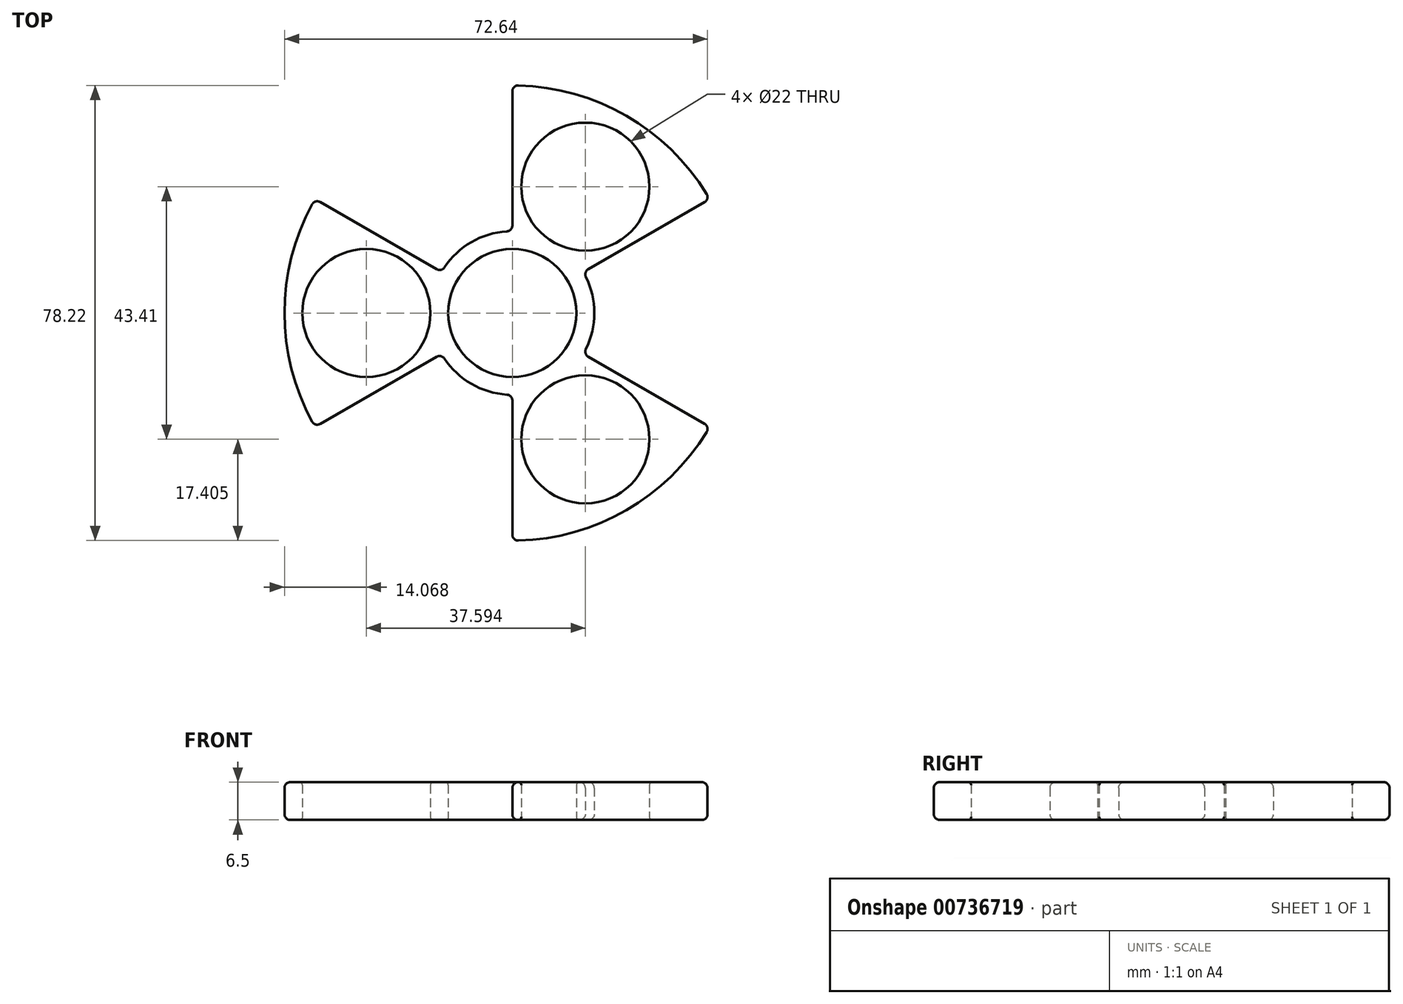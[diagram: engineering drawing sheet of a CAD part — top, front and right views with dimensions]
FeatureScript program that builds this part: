
annotation { "Feature Type Name" : "Feature", "Feature Type Description" : "" }
export const myFeature = defineFeature(function(context is Context, id is Id, definition is map)
    precondition{}
    {
        {
            var Q0;
            Q0=qCreatedBy(makeId("Top.planeOp"),FACE);
            var sketch = newSketch(context, id + "F0", { "sketchPlane" : qUnion([Q0])});
            skCircle(sketch, "E0", {"center": v(0, 0) * mm, "radius": 11 * mm});
            skCircle(sketch, "E1", {"center": v(0, 0) * mm, "radius": 40 * mm});
            skCircle(sketch, "E2", {"center": v(0, 0) * mm, "radius": 39.12 * mm});
            skLineSegment(sketch, "E3", {"start": v(0, 0) * mm, "end": v(0, 40) * mm});
            skLineSegment(sketch, "E4", {"start": v(9.53, -5.5) * mm, "end": v(34.64, -20) * mm});
            skLineSegment(sketch, "E5", {"start": v(-9.53, -5.5) * mm, "end": v(-34.64, -20) * mm});
            skLineSegment(sketch, "E6", {"start": v(-9.53, 5.5) * mm, "end": v(-34.64, 20) * mm});
            skLineSegment(sketch, "E7", {"start": v(9.53, 5.5) * mm, "end": v(34.64, 20) * mm});
            skLineSegment(sketch, "E8", {"start": v(0, 0) * mm, "end": v(0, -40) * mm});
            skCircle(sketch, "E9", {"center": v(0, 0) * mm, "radius": 25.06 * mm});
            skLineSegment(sketch, "E10", {"start": v(5.5, 9.53) * mm, "end": v(20, 34.64) * mm});
            skLineSegment(sketch, "E11", {"start": v(0, 0) * mm, "end": v(-53.49, 0) * mm});
            skLineSegment(sketch, "E12", {"start": v(5.5, -9.53) * mm, "end": v(20, -34.64) * mm});
            skCircle(sketch, "E13", {"center": v(12.53, 21.7) * mm, "radius": 11 * mm});
            skCircle(sketch, "E14", {"center": v(-25.06, 0) * mm, "radius": 11 * mm});
            skCircle(sketch, "E15", {"center": v(12.53, -21.7) * mm, "radius": 11 * mm});
            skPoint(sketch, "E15.perimeterSnap0", {"position": v(13.32, -23.08) * mm});
            skCircle(sketch, "E16", {"center": v(0, 0) * mm, "radius": 17.66 * mm});
            skCircle(sketch, "E17", {"center": v(0, 0) * mm, "radius": 14.06 * mm});
            skSolve(sketch);
        }
        {
            var Q0;
            {var subQ0=sQuery(id+"F0.wireOp",EDGE,"E11");var subQ1=sQuery(id+"F0.wireOp",EDGE,"E2");var subQ2=makeQuery(id+"F0.imprint","INTERSECT",VERTEX,{"derivedFrom":[subQ1,subQ0]});Q0=makeQuery(id+"F0.imprint","IMPRINT",FACE,{"disambiguationData":[TD([[makeQuery(id+"F0.imprint","IMPRINT",EDGE,{"disambiguationData":[TD([[subQ2,-1.0]])],"derivedFrom":subQ1}),1.0]])]});}
            var Q1;
            {var subQ1=sQuery(id+"F0.wireOp",EDGE,"E2");var subQ5=sQuery(id+"F0.wireOp",EDGE,"E6");var subQ6=makeQuery(id+"F0.imprint","INTERSECT",VERTEX,{"derivedFrom":[subQ1,subQ5]});Q1=makeQuery(id+"F0.imprint","IMPRINT",FACE,{"disambiguationData":[TD([[makeQuery(id+"F0.imprint","IMPRINT",EDGE,{"disambiguationData":[TD([[subQ6,-1.0]])],"derivedFrom":subQ1}),1.0]])]});}
            var Q2;
            {var subQ1=sQuery(id+"F0.wireOp",EDGE,"E6");var subQ5=sQuery(id+"F0.wireOp",EDGE,"E0");var subQ6=makeQuery(id+"F0.imprint","INTERSECT",VERTEX,{"derivedFrom":[subQ5,subQ1]});Q2=makeQuery(id+"F0.imprint","IMPRINT",FACE,{"disambiguationData":[TD([[makeQuery(id+"F0.imprint","IMPRINT",EDGE,{"disambiguationData":[TD([[subQ6,-1.0]])],"derivedFrom":subQ5}),-1.0]])]});}
            var Q3;
            {var subQ0=sQuery(id+"F0.wireOp",EDGE,"E11");var subQ1=sQuery(id+"F0.wireOp",EDGE,"E0");var subQ2=makeQuery(id+"F0.imprint","INTERSECT",VERTEX,{"derivedFrom":[subQ1,subQ0]});Q3=makeQuery(id+"F0.imprint","IMPRINT",FACE,{"disambiguationData":[TD([[makeQuery(id+"F0.imprint","IMPRINT",EDGE,{"disambiguationData":[TD([[subQ2,-1.0]])],"derivedFrom":subQ1}),-1.0]])]});}
            var Q4;
            {var subQ0=sQuery(id+"F0.wireOp",EDGE,"E10");var subQ1=sQuery(id+"F0.wireOp",EDGE,"E2");var subQ2=makeQuery(id+"F0.imprint","INTERSECT",VERTEX,{"derivedFrom":[subQ1,subQ0]});Q4=makeQuery(id+"F0.imprint","IMPRINT",FACE,{"disambiguationData":[TD([[makeQuery(id+"F0.imprint","IMPRINT",EDGE,{"disambiguationData":[TD([[subQ2,-1.0]])],"derivedFrom":subQ1}),1.0]])]});}
            var Q5;
            {var subQ5=sQuery(id+"F0.wireOp",EDGE,"E10");var subQ6=sQuery(id+"F0.wireOp",EDGE,"E2");var subQ7=makeQuery(id+"F0.imprint","INTERSECT",VERTEX,{"derivedFrom":[subQ6,subQ5]});Q5=makeQuery(id+"F0.imprint","IMPRINT",FACE,{"disambiguationData":[TD([[makeQuery(id+"F0.imprint","IMPRINT",EDGE,{"disambiguationData":[TD([[subQ7,1.0]])],"derivedFrom":subQ6}),1.0]])]});}
            var Q6;
            {var subQ0=sQuery(id+"F0.wireOp",EDGE,"E10");var subQ1=sQuery(id+"F0.wireOp",EDGE,"E0");var subQ2=makeQuery(id+"F0.imprint","INTERSECT",VERTEX,{"derivedFrom":[subQ1,subQ0]});Q6=makeQuery(id+"F0.imprint","IMPRINT",FACE,{"disambiguationData":[TD([[makeQuery(id+"F0.imprint","IMPRINT",EDGE,{"disambiguationData":[TD([[subQ2,1.0]])],"derivedFrom":subQ1}),-1.0]])]});}
            var Q7;
            {var subQ0=sQuery(id+"F0.wireOp",EDGE,"E10");var subQ1=sQuery(id+"F0.wireOp",EDGE,"E0");var subQ2=makeQuery(id+"F0.imprint","INTERSECT",VERTEX,{"derivedFrom":[subQ1,subQ0]});Q7=makeQuery(id+"F0.imprint","IMPRINT",FACE,{"disambiguationData":[TD([[makeQuery(id+"F0.imprint","IMPRINT",EDGE,{"disambiguationData":[TD([[subQ2,-1.0]])],"derivedFrom":subQ1}),-1.0]])]});}
            var Q8;
            {var subQ0=sQuery(id+"F0.wireOp",EDGE,"E12");var subQ1=sQuery(id+"F0.wireOp",EDGE,"E0");var subQ2=makeQuery(id+"F0.imprint","INTERSECT",VERTEX,{"derivedFrom":[subQ1,subQ0]});Q8=makeQuery(id+"F0.imprint","IMPRINT",FACE,{"disambiguationData":[TD([[makeQuery(id+"F0.imprint","IMPRINT",EDGE,{"disambiguationData":[TD([[subQ2,-1.0]])],"derivedFrom":subQ1}),-1.0]])]});}
            var Q9;
            {var subQ1=sQuery(id+"F0.wireOp",EDGE,"E0");var subQ5=sQuery(id+"F0.wireOp",EDGE,"E8");var subQ6=makeQuery(id+"F0.imprint","INTERSECT",VERTEX,{"derivedFrom":[subQ1,subQ5]});Q9=makeQuery(id+"F0.imprint","IMPRINT",FACE,{"disambiguationData":[TD([[makeQuery(id+"F0.imprint","IMPRINT",EDGE,{"disambiguationData":[TD([[subQ6,-1.0]])],"derivedFrom":subQ1}),-1.0]])]});}
            var Q10;
            {var subQ1=sQuery(id+"F0.wireOp",EDGE,"E2");var subQ5=sQuery(id+"F0.wireOp",EDGE,"E8");var subQ6=makeQuery(id+"F0.imprint","INTERSECT",VERTEX,{"derivedFrom":[subQ1,subQ5]});Q10=makeQuery(id+"F0.imprint","IMPRINT",FACE,{"disambiguationData":[TD([[makeQuery(id+"F0.imprint","IMPRINT",EDGE,{"disambiguationData":[TD([[subQ6,-1.0]])],"derivedFrom":subQ1}),1.0]])]});}
            var Q11;
            {var subQ0=sQuery(id+"F0.wireOp",EDGE,"E3");var subQ1=sQuery(id+"F0.wireOp",EDGE,"E0");var subQ2=makeQuery(id+"F0.imprint","INTERSECT",VERTEX,{"derivedFrom":[subQ1,subQ0]});Q11=makeQuery(id+"F0.imprint","IMPRINT",FACE,{"disambiguationData":[TD([[makeQuery(id+"F0.imprint","IMPRINT",EDGE,{"disambiguationData":[TD([[subQ2,-1.0]])],"derivedFrom":subQ1}),-1.0]])]});}
            var Q12;
            {var subQ0=sQuery(id+"F0.wireOp",EDGE,"E5");var subQ1=sQuery(id+"F0.wireOp",EDGE,"E0");var subQ2=makeQuery(id+"F0.imprint","INTERSECT",VERTEX,{"derivedFrom":[subQ1,subQ0]});Q12=makeQuery(id+"F0.imprint","IMPRINT",FACE,{"disambiguationData":[TD([[makeQuery(id+"F0.imprint","IMPRINT",EDGE,{"disambiguationData":[TD([[subQ2,-1.0]])],"derivedFrom":subQ1}),-1.0]])]});}
            var Q13;
            {var subQ0=sQuery(id+"F0.wireOp",EDGE,"E7");var subQ1=sQuery(id+"F0.wireOp",EDGE,"E0");var subQ2=makeQuery(id+"F0.imprint","INTERSECT",VERTEX,{"derivedFrom":[subQ1,subQ0]});Q13=makeQuery(id+"F0.imprint","IMPRINT",FACE,{"disambiguationData":[TD([[makeQuery(id+"F0.imprint","IMPRINT",EDGE,{"disambiguationData":[TD([[subQ2,1.0]])],"derivedFrom":subQ1}),-1.0]])]});}
            var Q14;
            {var subQ0=sQuery(id+"F0.wireOp",EDGE,"E12");var subQ1=sQuery(id+"F0.wireOp",EDGE,"E2");var subQ2=makeQuery(id+"F0.imprint","INTERSECT",VERTEX,{"derivedFrom":[subQ1,subQ0]});Q14=makeQuery(id+"F0.imprint","IMPRINT",FACE,{"disambiguationData":[TD([[makeQuery(id+"F0.imprint","IMPRINT",EDGE,{"disambiguationData":[TD([[subQ2,-1.0]])],"derivedFrom":subQ1}),1.0]])]});}
            var Q15;
            {var subQ0=sQuery(id+"F0.wireOp",EDGE,"E16");var subQ1=sQuery(id+"F0.wireOp",EDGE,"E6");var subQ2=makeQuery(id+"F0.imprint","INTERSECT",VERTEX,{"derivedFrom":[subQ1,subQ0]});Q15=makeQuery(id+"F0.imprint","IMPRINT",FACE,{"disambiguationData":[TD([[makeQuery(id+"F0.imprint","IMPRINT",EDGE,{"disambiguationData":[TD([[subQ2,-1.0]])],"derivedFrom":subQ1}),1.0]])]});}
            var Q16;
            {var subQ0=sQuery(id+"F0.wireOp",EDGE,"E17");var subQ1=sQuery(id+"F0.wireOp",EDGE,"E6");var subQ2=makeQuery(id+"F0.imprint","INTERSECT",VERTEX,{"derivedFrom":[subQ1,subQ0]});Q16=makeQuery(id+"F0.imprint","IMPRINT",FACE,{"disambiguationData":[TD([[makeQuery(id+"F0.imprint","IMPRINT",EDGE,{"disambiguationData":[TD([[subQ2,-1.0]])],"derivedFrom":subQ1}),1.0]])]});}
            var Q17;
            {var subQ0=sQuery(id+"F0.wireOp",EDGE,"E16");var subQ1=sQuery(id+"F0.wireOp",EDGE,"E5");var subQ2=makeQuery(id+"F0.imprint","INTERSECT",VERTEX,{"derivedFrom":[subQ1,subQ0]});Q17=makeQuery(id+"F0.imprint","IMPRINT",FACE,{"disambiguationData":[TD([[makeQuery(id+"F0.imprint","IMPRINT",EDGE,{"disambiguationData":[TD([[subQ2,-1.0]])],"derivedFrom":subQ1}),-1.0]])]});}
            var Q18;
            {var subQ0=sQuery(id+"F0.wireOp",EDGE,"E17");var subQ1=sQuery(id+"F0.wireOp",EDGE,"E5");var subQ2=makeQuery(id+"F0.imprint","INTERSECT",VERTEX,{"derivedFrom":[subQ1,subQ0]});Q18=makeQuery(id+"F0.imprint","IMPRINT",FACE,{"disambiguationData":[TD([[makeQuery(id+"F0.imprint","IMPRINT",EDGE,{"disambiguationData":[TD([[subQ2,-1.0]])],"derivedFrom":subQ1}),-1.0]])]});}
            var Q19;
            {var subQ0=sQuery(id+"F0.wireOp",EDGE,"E16");var subQ1=sQuery(id+"F0.wireOp",EDGE,"E7");var subQ2=makeQuery(id+"F0.imprint","INTERSECT",VERTEX,{"derivedFrom":[subQ1,subQ0]});Q19=makeQuery(id+"F0.imprint","IMPRINT",FACE,{"disambiguationData":[TD([[makeQuery(id+"F0.imprint","IMPRINT",EDGE,{"disambiguationData":[TD([[subQ2,-1.0]])],"derivedFrom":subQ1}),1.0]])]});}
            var Q20;
            {var subQ0=sQuery(id+"F0.wireOp",EDGE,"E17");var subQ1=sQuery(id+"F0.wireOp",EDGE,"E7");var subQ2=makeQuery(id+"F0.imprint","INTERSECT",VERTEX,{"derivedFrom":[subQ1,subQ0]});Q20=makeQuery(id+"F0.imprint","IMPRINT",FACE,{"disambiguationData":[TD([[makeQuery(id+"F0.imprint","IMPRINT",EDGE,{"disambiguationData":[TD([[subQ2,-1.0]])],"derivedFrom":subQ1}),1.0]])]});}
            var Q21;
            {var subQ0=sQuery(id+"F0.wireOp",EDGE,"E17");var subQ1=sQuery(id+"F0.wireOp",EDGE,"E3");var subQ2=makeQuery(id+"F0.imprint","INTERSECT",VERTEX,{"derivedFrom":[subQ1,subQ0]});Q21=makeQuery(id+"F0.imprint","IMPRINT",FACE,{"disambiguationData":[TD([[makeQuery(id+"F0.imprint","IMPRINT",EDGE,{"disambiguationData":[TD([[subQ2,-1.0]])],"derivedFrom":subQ1}),-1.0]])]});}
            var Q22;
            {var subQ0=sQuery(id+"F0.wireOp",EDGE,"E16");var subQ1=sQuery(id+"F0.wireOp",EDGE,"E3");var subQ2=makeQuery(id+"F0.imprint","INTERSECT",VERTEX,{"derivedFrom":[subQ1,subQ0]});Q22=makeQuery(id+"F0.imprint","IMPRINT",FACE,{"disambiguationData":[TD([[makeQuery(id+"F0.imprint","IMPRINT",EDGE,{"disambiguationData":[TD([[subQ2,-1.0]])],"derivedFrom":subQ1}),-1.0]])]});}
            var Q23;
            {var subQ0=sQuery(id+"F0.wireOp",EDGE,"E17");var subQ1=sQuery(id+"F0.wireOp",EDGE,"E4");var subQ2=makeQuery(id+"F0.imprint","INTERSECT",VERTEX,{"derivedFrom":[subQ1,subQ0]});Q23=makeQuery(id+"F0.imprint","IMPRINT",FACE,{"disambiguationData":[TD([[makeQuery(id+"F0.imprint","IMPRINT",EDGE,{"disambiguationData":[TD([[subQ2,-1.0]])],"derivedFrom":subQ1}),-1.0]])]});}
            var Q24;
            {var subQ0=sQuery(id+"F0.wireOp",EDGE,"E16");var subQ1=sQuery(id+"F0.wireOp",EDGE,"E4");var subQ2=makeQuery(id+"F0.imprint","INTERSECT",VERTEX,{"derivedFrom":[subQ1,subQ0]});Q24=makeQuery(id+"F0.imprint","IMPRINT",FACE,{"disambiguationData":[TD([[makeQuery(id+"F0.imprint","IMPRINT",EDGE,{"disambiguationData":[TD([[subQ2,-1.0]])],"derivedFrom":subQ1}),-1.0]])]});}
            var Q25;
            {var subQ0=sQuery(id+"F0.wireOp",EDGE,"E17");var subQ1=sQuery(id+"F0.wireOp",EDGE,"E8");var subQ2=makeQuery(id+"F0.imprint","INTERSECT",VERTEX,{"derivedFrom":[subQ1,subQ0]});Q25=makeQuery(id+"F0.imprint","IMPRINT",FACE,{"disambiguationData":[TD([[makeQuery(id+"F0.imprint","IMPRINT",EDGE,{"disambiguationData":[TD([[subQ2,-1.0]])],"derivedFrom":subQ1}),1.0]])]});}
            var Q26;
            {var subQ0=sQuery(id+"F0.wireOp",EDGE,"E16");var subQ1=sQuery(id+"F0.wireOp",EDGE,"E8");var subQ2=makeQuery(id+"F0.imprint","INTERSECT",VERTEX,{"derivedFrom":[subQ1,subQ0]});Q26=makeQuery(id+"F0.imprint","IMPRINT",FACE,{"disambiguationData":[TD([[makeQuery(id+"F0.imprint","IMPRINT",EDGE,{"disambiguationData":[TD([[subQ2,-1.0]])],"derivedFrom":subQ1}),1.0]])]});}
            extrude(context, id + "F1", {"entities" : qUnion([Q0, Q1, Q2, Q3, Q4, Q5, Q6, Q7, Q8, Q9, Q10, Q11, Q12, Q13, Q14, Q15, Q16, Q17, Q18, Q19, Q20, Q21, Q22, Q23, Q24, Q25, Q26]), "depth" : 6.5 * mm, "offsetDistance" : 25 * mm});
        }
        {
            var Q0;
            Q0=makeQuery(id+"F1.opExtrude","SWEPT_EDGE",EDGE,{"disambiguationData":[OSD([sQuery(id+"F0.wireOp",EDGE,"E2"),sQuery(id+"F0.wireOp",EDGE,"E5")])]});
            var Q1;
            Q1=makeQuery(id+"F1.opExtrude","CAP_EDGE",EDGE,{"disambiguationData":[OSD([sQuery(id+"F0.wireOp",EDGE,"E7")])],"isStart":false});
            var Q2;
            Q2=makeQuery(id+"F1.opExtrude","SWEPT_EDGE",EDGE,{"disambiguationData":[OSD([sQuery(id+"F0.wireOp",EDGE,"E3"),sQuery(id+"F0.wireOp",EDGE,"E17")])]});
            var Q3;
            Q3=makeQuery(id+"F1.opExtrude","CAP_EDGE",EDGE,{"disambiguationData":[OSD([sQuery(id+"F0.wireOp",EDGE,"E5")])],"isStart":false});
            var Q4;
            Q4=makeQuery(id+"F1.opExtrude","SWEPT_EDGE",EDGE,{"disambiguationData":[OSD([sQuery(id+"F0.wireOp",EDGE,"E2"),sQuery(id+"F0.wireOp",EDGE,"E6")])]});
            var Q5;
            Q5=makeQuery(id+"F1.opExtrude","CAP_EDGE",EDGE,{"disambiguationData":[OSD([sQuery(id+"F0.wireOp",EDGE,"E8")])],"isStart":false});
            var Q6;
            Q6=makeQuery(id+"F1.opExtrude","SWEPT_EDGE",EDGE,{"disambiguationData":[OSD([sQuery(id+"F0.wireOp",EDGE,"E2"),sQuery(id+"F0.wireOp",EDGE,"E3")])]});
            var Q7;
            Q7=makeQuery(id+"F1.opExtrude","CAP_EDGE",EDGE,{"disambiguationData":[OSD([sQuery(id+"F0.wireOp",EDGE,"E8")])],"isStart":true});
            var Q8;
            {var subQ0=sQuery(id+"F0.wireOp",EDGE,"E17");Q8=makeQuery(id+"F1.opExtrude","CAP_EDGE",EDGE,{"disambiguationData":[OSD([subQ0]),TDD([makeQuery(id+"F0.imprint","IMPRINT",EDGE,{"disambiguationData":[TD([[makeQuery(id+"F0.imprint","INTERSECT",VERTEX,{"derivedFrom":[sQuery(id+"F0.wireOp",EDGE,"E3"),subQ0]}),-1.0]])],"derivedFrom":subQ0})])],"isStart":false});}
            var Q9;
            {var subQ0=sQuery(id+"F0.wireOp",EDGE,"E2");var subQ1=makeQuery(id+"F0.imprint","INTERSECT",VERTEX,{"derivedFrom":[subQ0,sQuery(id+"F0.wireOp",EDGE,"E12")]});Q9=makeQuery(id+"F1.opExtrude","CAP_EDGE",EDGE,{"disambiguationData":[OSD([subQ0]),TDD([makeQuery(id+"F0.imprint","IMPRINT",EDGE,{"disambiguationData":[TD([[makeQuery(id+"F0.imprint","INTERSECT",VERTEX,{"derivedFrom":[subQ0,sQuery(id+"F0.wireOp",EDGE,"E8")]}),-1.0]])],"derivedFrom":subQ0}),makeQuery(id+"F0.imprint","IMPRINT",EDGE,{"disambiguationData":[TD([[subQ1,-1.0]])],"derivedFrom":subQ0})])],"isStart":false});}
            var Q10;
            {var subQ0=sQuery(id+"F0.wireOp",EDGE,"E17");Q10=makeQuery(id+"F1.opExtrude","CAP_EDGE",EDGE,{"disambiguationData":[OSD([subQ0]),TDD([makeQuery(id+"F0.imprint","IMPRINT",EDGE,{"disambiguationData":[TD([[makeQuery(id+"F0.imprint","INTERSECT",VERTEX,{"derivedFrom":[sQuery(id+"F0.wireOp",EDGE,"E4"),subQ0]}),-1.0]])],"derivedFrom":subQ0})])],"isStart":false});}
            var Q11;
            {var subQ0=sQuery(id+"F0.wireOp",EDGE,"E17");Q11=makeQuery(id+"F1.opExtrude","CAP_EDGE",EDGE,{"disambiguationData":[OSD([subQ0]),TDD([makeQuery(id+"F0.imprint","IMPRINT",EDGE,{"disambiguationData":[TD([[makeQuery(id+"F0.imprint","INTERSECT",VERTEX,{"derivedFrom":[sQuery(id+"F0.wireOp",EDGE,"E3"),subQ0]}),-1.0]])],"derivedFrom":subQ0})])],"isStart":true});}
            var Q12;
            {var subQ0=sQuery(id+"F0.wireOp",EDGE,"E17");Q12=makeQuery(id+"F1.opExtrude","CAP_EDGE",EDGE,{"disambiguationData":[OSD([subQ0]),TDD([makeQuery(id+"F0.imprint","IMPRINT",EDGE,{"disambiguationData":[TD([[makeQuery(id+"F0.imprint","INTERSECT",VERTEX,{"derivedFrom":[sQuery(id+"F0.wireOp",EDGE,"E5"),subQ0]}),-1.0]])],"derivedFrom":subQ0})])],"isStart":false});}
            var Q13;
            {var subQ0=sQuery(id+"F0.wireOp",EDGE,"E2");var subQ1=makeQuery(id+"F0.imprint","INTERSECT",VERTEX,{"derivedFrom":[subQ0,sQuery(id+"F0.wireOp",EDGE,"E11")]});Q13=makeQuery(id+"F1.opExtrude","CAP_EDGE",EDGE,{"disambiguationData":[OSD([subQ0]),TDD([makeQuery(id+"F0.imprint","IMPRINT",EDGE,{"disambiguationData":[TD([[makeQuery(id+"F0.imprint","INTERSECT",VERTEX,{"derivedFrom":[subQ0,sQuery(id+"F0.wireOp",EDGE,"E6")]}),-1.0]])],"derivedFrom":subQ0}),makeQuery(id+"F0.imprint","IMPRINT",EDGE,{"disambiguationData":[TD([[subQ1,-1.0]])],"derivedFrom":subQ0})])],"isStart":false});}
            var Q14;
            {var subQ0=sQuery(id+"F0.wireOp",EDGE,"E2");var subQ1=makeQuery(id+"F0.imprint","INTERSECT",VERTEX,{"derivedFrom":[subQ0,sQuery(id+"F0.wireOp",EDGE,"E11")]});Q14=makeQuery(id+"F1.opExtrude","CAP_EDGE",EDGE,{"disambiguationData":[OSD([subQ0]),TDD([makeQuery(id+"F0.imprint","IMPRINT",EDGE,{"disambiguationData":[TD([[makeQuery(id+"F0.imprint","INTERSECT",VERTEX,{"derivedFrom":[subQ0,sQuery(id+"F0.wireOp",EDGE,"E6")]}),-1.0]])],"derivedFrom":subQ0}),makeQuery(id+"F0.imprint","IMPRINT",EDGE,{"disambiguationData":[TD([[subQ1,-1.0]])],"derivedFrom":subQ0})])],"isStart":true});}
            var Q15;
            Q15=makeQuery(id+"F1.opExtrude","CAP_EDGE",EDGE,{"disambiguationData":[OSD([sQuery(id+"F0.wireOp",EDGE,"E3")])],"isStart":true});
            var Q16;
            {var subQ0=sQuery(id+"F0.wireOp",EDGE,"E2");var subQ1=makeQuery(id+"F0.imprint","INTERSECT",VERTEX,{"derivedFrom":[subQ0,sQuery(id+"F0.wireOp",EDGE,"E10")]});Q16=makeQuery(id+"F1.opExtrude","CAP_EDGE",EDGE,{"disambiguationData":[OSD([subQ0]),TDD([makeQuery(id+"F0.imprint","IMPRINT",EDGE,{"disambiguationData":[TD([[subQ1,1.0]])],"derivedFrom":subQ0}),makeQuery(id+"F0.imprint","IMPRINT",EDGE,{"disambiguationData":[TD([[subQ1,-1.0]])],"derivedFrom":subQ0})])],"isStart":false});}
            var Q17;
            {var subQ0=sQuery(id+"F0.wireOp",EDGE,"E2");var subQ1=makeQuery(id+"F0.imprint","INTERSECT",VERTEX,{"derivedFrom":[subQ0,sQuery(id+"F0.wireOp",EDGE,"E10")]});Q17=makeQuery(id+"F1.opExtrude","CAP_EDGE",EDGE,{"disambiguationData":[OSD([subQ0]),TDD([makeQuery(id+"F0.imprint","IMPRINT",EDGE,{"disambiguationData":[TD([[subQ1,1.0]])],"derivedFrom":subQ0}),makeQuery(id+"F0.imprint","IMPRINT",EDGE,{"disambiguationData":[TD([[subQ1,-1.0]])],"derivedFrom":subQ0})])],"isStart":true});}
            var Q18;
            Q18=makeQuery(id+"F1.opExtrude","CAP_EDGE",EDGE,{"disambiguationData":[OSD([sQuery(id+"F0.wireOp",EDGE,"E3")])],"isStart":false});
            var Q19;
            Q19=makeQuery(id+"F1.opExtrude","SWEPT_EDGE",EDGE,{"disambiguationData":[OSD([sQuery(id+"F0.wireOp",EDGE,"E4"),sQuery(id+"F0.wireOp",EDGE,"E17")])]});
            var Q20;
            Q20=makeQuery(id+"F1.opExtrude","CAP_EDGE",EDGE,{"disambiguationData":[OSD([sQuery(id+"F0.wireOp",EDGE,"E4")])],"isStart":false});
            var Q21;
            Q21=makeQuery(id+"F1.opExtrude","SWEPT_EDGE",EDGE,{"disambiguationData":[OSD([sQuery(id+"F0.wireOp",EDGE,"E5"),sQuery(id+"F0.wireOp",EDGE,"E17")])]});
            var Q22;
            {var subQ0=sQuery(id+"F0.wireOp",EDGE,"E17");Q22=makeQuery(id+"F1.opExtrude","CAP_EDGE",EDGE,{"disambiguationData":[OSD([subQ0]),TDD([makeQuery(id+"F0.imprint","IMPRINT",EDGE,{"disambiguationData":[TD([[makeQuery(id+"F0.imprint","INTERSECT",VERTEX,{"derivedFrom":[sQuery(id+"F0.wireOp",EDGE,"E4"),subQ0]}),-1.0]])],"derivedFrom":subQ0})])],"isStart":true});}
            var Q23;
            Q23=makeQuery(id+"F1.opExtrude","CAP_EDGE",EDGE,{"disambiguationData":[OSD([sQuery(id+"F0.wireOp",EDGE,"E6")])],"isStart":true});
            var Q24;
            {var subQ0=sQuery(id+"F0.wireOp",EDGE,"E17");Q24=makeQuery(id+"F1.opExtrude","CAP_EDGE",EDGE,{"disambiguationData":[OSD([subQ0]),TDD([makeQuery(id+"F0.imprint","IMPRINT",EDGE,{"disambiguationData":[TD([[makeQuery(id+"F0.imprint","INTERSECT",VERTEX,{"derivedFrom":[sQuery(id+"F0.wireOp",EDGE,"E5"),subQ0]}),-1.0]])],"derivedFrom":subQ0})])],"isStart":true});}
            var Q25;
            Q25=makeQuery(id+"F1.opExtrude","CAP_EDGE",EDGE,{"disambiguationData":[OSD([sQuery(id+"F0.wireOp",EDGE,"E7")])],"isStart":true});
            var Q26;
            Q26=makeQuery(id+"F1.opExtrude","SWEPT_EDGE",EDGE,{"disambiguationData":[OSD([sQuery(id+"F0.wireOp",EDGE,"E8"),sQuery(id+"F0.wireOp",EDGE,"E17")])]});
            var Q27;
            Q27=makeQuery(id+"F1.opExtrude","CAP_EDGE",EDGE,{"disambiguationData":[OSD([sQuery(id+"F0.wireOp",EDGE,"E6")])],"isStart":false});
            var Q28;
            Q28=makeQuery(id+"F1.opExtrude","SWEPT_EDGE",EDGE,{"disambiguationData":[OSD([sQuery(id+"F0.wireOp",EDGE,"E6"),sQuery(id+"F0.wireOp",EDGE,"E17")])]});
            var Q29;
            Q29=makeQuery(id+"F1.opExtrude","SWEPT_EDGE",EDGE,{"disambiguationData":[OSD([sQuery(id+"F0.wireOp",EDGE,"E2"),sQuery(id+"F0.wireOp",EDGE,"E8")])]});
            var Q30;
            Q30=makeQuery(id+"F1.opExtrude","SWEPT_EDGE",EDGE,{"disambiguationData":[OSD([sQuery(id+"F0.wireOp",EDGE,"E7"),sQuery(id+"F0.wireOp",EDGE,"E17")])]});
            var Q31;
            Q31=makeQuery(id+"F1.opExtrude","SWEPT_EDGE",EDGE,{"disambiguationData":[OSD([sQuery(id+"F0.wireOp",EDGE,"E2"),sQuery(id+"F0.wireOp",EDGE,"E7")])]});
            var Q32;
            {var subQ0=sQuery(id+"F0.wireOp",EDGE,"E2");var subQ1=makeQuery(id+"F0.imprint","INTERSECT",VERTEX,{"derivedFrom":[subQ0,sQuery(id+"F0.wireOp",EDGE,"E12")]});Q32=makeQuery(id+"F1.opExtrude","CAP_EDGE",EDGE,{"disambiguationData":[OSD([subQ0]),TDD([makeQuery(id+"F0.imprint","IMPRINT",EDGE,{"disambiguationData":[TD([[makeQuery(id+"F0.imprint","INTERSECT",VERTEX,{"derivedFrom":[subQ0,sQuery(id+"F0.wireOp",EDGE,"E8")]}),-1.0]])],"derivedFrom":subQ0}),makeQuery(id+"F0.imprint","IMPRINT",EDGE,{"disambiguationData":[TD([[subQ1,-1.0]])],"derivedFrom":subQ0})])],"isStart":true});}
            var Q33;
            Q33=makeQuery(id+"F1.opExtrude","CAP_EDGE",EDGE,{"disambiguationData":[OSD([sQuery(id+"F0.wireOp",EDGE,"E5")])],"isStart":true});
            var Q34;
            Q34=makeQuery(id+"F1.opExtrude","SWEPT_EDGE",EDGE,{"disambiguationData":[OSD([sQuery(id+"F0.wireOp",EDGE,"E2"),sQuery(id+"F0.wireOp",EDGE,"E4")])]});
            var Q35;
            Q35=makeQuery(id+"F1.opExtrude","CAP_EDGE",EDGE,{"disambiguationData":[OSD([sQuery(id+"F0.wireOp",EDGE,"E4")])],"isStart":true});
            fillet(context, id + "F2", {"entities" : qUnion([Q0, Q1, Q2, Q3, Q4, Q5, Q6, Q7, Q8, Q9, Q10, Q11, Q12, Q13, Q14, Q15, Q16, Q17, Q18, Q19, Q20, Q21, Q22, Q23, Q24, Q25, Q26, Q27, Q28, Q29, Q30, Q31, Q32, Q33, Q34, Q35]), "radius" : 1 * mm, "tangentPropagation" : true, "allowEdgeOverflow" : false});
        }
        {
            var Q0;
            Q0=makeQuery(id+"F1.opExtrude","CAP_EDGE",EDGE,{"disambiguationData":[OSD([sQuery(id+"F0.wireOp",EDGE,"E14")])],"isStart":true});
            var Q1;
            Q1=makeQuery(id+"F1.opExtrude","CAP_EDGE",EDGE,{"disambiguationData":[OSD([sQuery(id+"F0.wireOp",EDGE,"E0")])],"isStart":true});
            var Q2;
            Q2=makeQuery(id+"F1.opExtrude","CAP_EDGE",EDGE,{"disambiguationData":[OSD([sQuery(id+"F0.wireOp",EDGE,"E15")])],"isStart":true});
            var Q3;
            Q3=makeQuery(id+"F1.opExtrude","CAP_EDGE",EDGE,{"disambiguationData":[OSD([sQuery(id+"F0.wireOp",EDGE,"E13")])],"isStart":true});
            var Q4;
            Q4=makeQuery(id+"F1.opExtrude","CAP_EDGE",EDGE,{"disambiguationData":[OSD([sQuery(id+"F0.wireOp",EDGE,"E15")])],"isStart":false});
            var Q5;
            Q5=makeQuery(id+"F1.opExtrude","CAP_EDGE",EDGE,{"disambiguationData":[OSD([sQuery(id+"F0.wireOp",EDGE,"E0")])],"isStart":false});
            var Q6;
            Q6=makeQuery(id+"F1.opExtrude","CAP_EDGE",EDGE,{"disambiguationData":[OSD([sQuery(id+"F0.wireOp",EDGE,"E14")])],"isStart":false});
            var Q7;
            Q7=makeQuery(id+"F1.opExtrude","CAP_EDGE",EDGE,{"disambiguationData":[OSD([sQuery(id+"F0.wireOp",EDGE,"E13")])],"isStart":false});
            fillet(context, id + "F3", {"entities" : qUnion([Q0, Q1, Q2, Q3, Q4, Q5, Q6, Q7]), "radius" : 0.5 * mm, "tangentPropagation" : true, "allowEdgeOverflow" : false});
        }
    });
